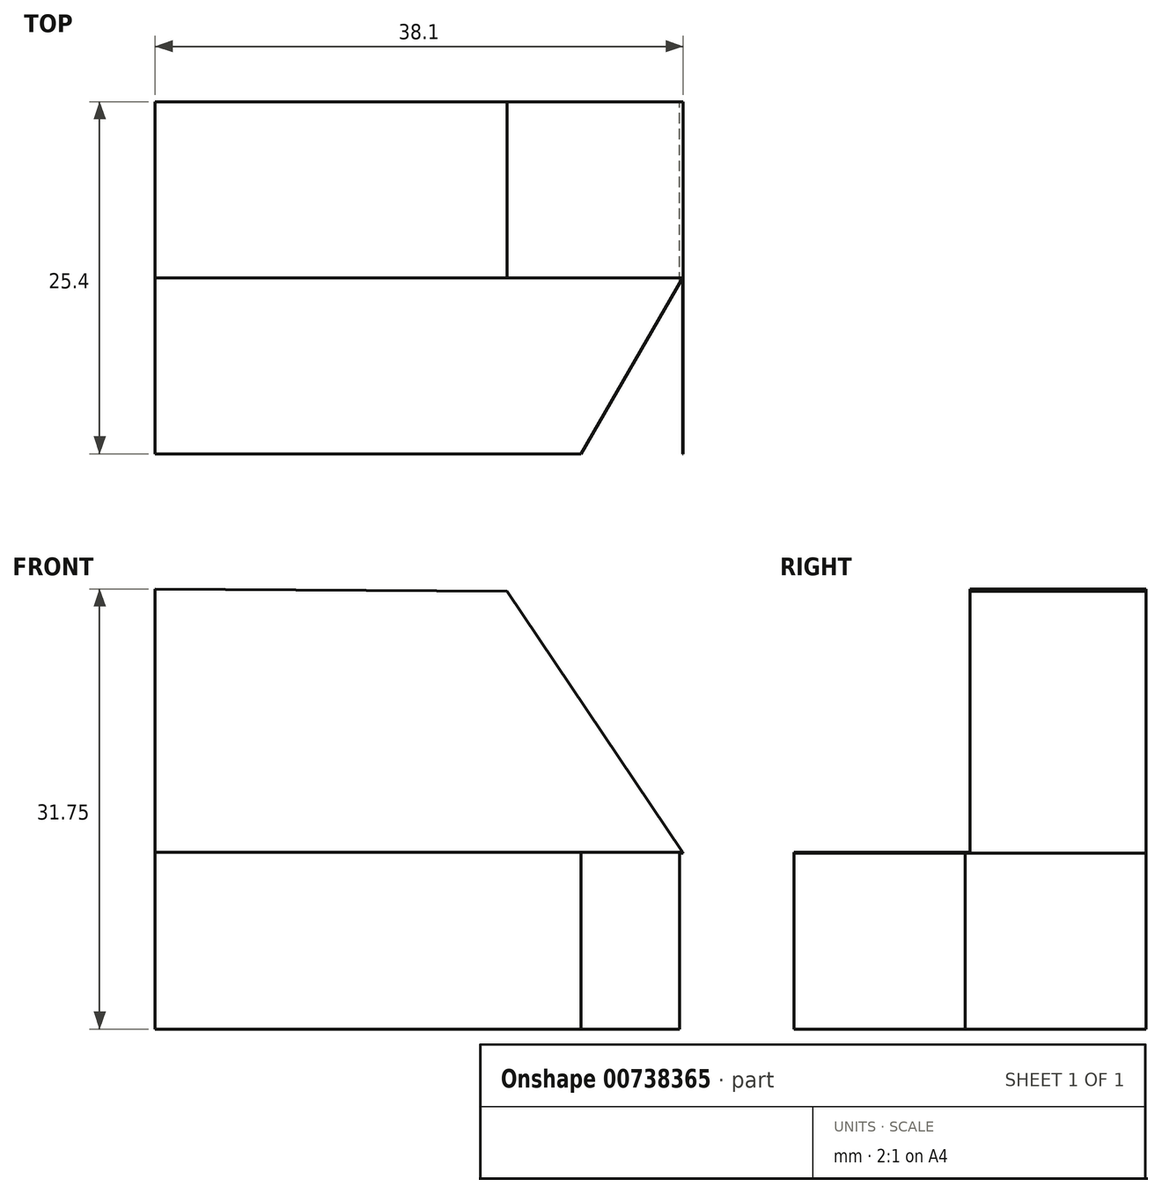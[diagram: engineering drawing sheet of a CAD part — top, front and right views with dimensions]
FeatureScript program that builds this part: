
annotation { "Feature Type Name" : "Feature", "Feature Type Description" : "" }
export const myFeature = defineFeature(function(context is Context, id is Id, definition is map)
    precondition{}
    {
        {
            var Q0;
            Q0=qCreatedBy(makeId("Front.planeOp"),FACE);
            var sketch = newSketch(context, id + "F0", { "sketchPlane" : qUnion([Q0])});
            skLineSegment(sketch, "E0", {"start": v(0, 31.75) * mm, "end": v(0, 0) * mm});
            skLineSegment(sketch, "E1", {"start": v(0, 0) * mm, "end": v(38.1, 0) * mm});
            skLineSegment(sketch, "E2", {"start": v(38.1, 0) * mm, "end": v(38.1, 12.7) * mm});
            skLineSegment(sketch, "E3", {"start": v(38.1, 12.7) * mm, "end": v(25.4, 31.59) * mm});
            skLineSegment(sketch, "E4", {"start": v(25.4, 31.59) * mm, "end": v(0, 31.75) * mm});
            skSolve(sketch);
        }
        {
            var Q0;
            Q0 = qSketchRegion(id + "F0", true);
            extrude(context, id + "F1", {"entities" : qUnion([Q0]), "depth" : 25.4 * mm, "offsetDistance" : 25.4 * mm});
        }
        {
            var Q0;
            Q0=qCreatedBy(makeId("Right.planeOp"),FACE);
            var sketch = newSketch(context, id + "F2", { "sketchPlane" : qUnion([Q0])});
            skLineSegment(sketch, "E5", {"start": v(-25.59, 31.92) * mm, "end": v(-12.92, 31.92) * mm});
            skLineSegment(sketch, "E6", {"start": v(-12.92, 31.92) * mm, "end": v(-12.92, 12.69) * mm});
            skLineSegment(sketch, "E7", {"start": v(-12.92, 12.69) * mm, "end": v(-25.4, 12.69) * mm});
            skLineSegment(sketch, "E8", {"start": v(-25.4, 12.69) * mm, "end": v(-25.59, 31.92) * mm});
            skSolve(sketch);
        }
        {
            var Q0;
            Q0=makeQuery(id+"F2.imprint","IMPRINT",FACE,{"disambiguationData":[TD([[makeQuery(id+"F2.imprint","IMPRINT",EDGE,{"derivedFrom":sQuery(id+"F2.wireOp",EDGE,"E5")}),-1.0]])]});
            extrude(context, id + "F3", {"entities" : qUnion([Q0]), "operationType" : NewBodyOperationType.REMOVE, "endBound" : BoundingType.THROUGH_ALL, "oppositeDirection" : true, "depth" : 25.4 * mm, "offsetDistance" : 25.4 * mm});
        }
        {
            var Q0;
            Q0 = qSketchRegion(id + "F2", true);
            var Q1;
            Q1=makeQuery(id+"F1.opExtrude","SWEPT_FACE",FACE,{"disambiguationData":[OSD([sQuery(id+"F0.wireOp",EDGE,"E0")])]});
            extrude(context, id + "F4", {"entities" : qUnion([Q0, Q1]), "operationType" : NewBodyOperationType.REMOVE, "oppositeDirection" : true, "depth" : 25.4 * mm, "offsetDistance" : 25.4 * mm});
        }
        {
            var Q0;
            Q0=makeQuery(id+"F1.opExtrude","SWEPT_FACE",FACE,{"disambiguationData":[OSD([sQuery(id+"F0.wireOp",EDGE,"E0")])]});
            var sketch = newSketch(context, id + "F5", { "sketchPlane" : qUnion([Q0])});
            skLineSegment(sketch, "E9", {"start": v(12.7, 31.75) * mm, "end": v(12.7, 12.77) * mm});
            skLineSegment(sketch, "E10", {"start": v(12.7, 12.77) * mm, "end": v(26.84, 12.77) * mm});
            skSolve(sketch);
        }
        {
            var Q0;
            Q0 = qSketchRegion(id + "F5", true);
            var Q1;
            {var subQ0=sQuery(id+"F5.wireOp",EDGE,"E9");Q1=makeQuery(id+"F5.imprint","IMPRINT",FACE,{"disambiguationData":[TD([[makeQuery(id+"F5.imprint","IMPRINT",EDGE,{"derivedFrom":subQ0}),1.0]])]});}
            extrude(context, id + "F6", {"entities" : qUnion([Q0, Q1]), "operationType" : NewBodyOperationType.REMOVE, "endBound" : BoundingType.THROUGH_ALL, "oppositeDirection" : true, "depth" : 25.4 * mm, "offsetDistance" : 25.4 * mm});
        }
        {
            var Q0;
            Q0=makeQuery(id+"F6.boolean.opBoolean","COPY",FACE,{"derivedFrom":makeQuery(id+"F6.opExtrude","SWEPT_FACE",FACE,{"disambiguationData":[OSD([sQuery(id+"F5.wireOp",EDGE,"E10")])]})});
            var sketch = newSketch(context, id + "F7", { "sketchPlane" : qUnion([Q0])});
            skLineSegment(sketch, "E11", {"start": v(38.06, -12.7) * mm, "end": v(30.73, -25.4) * mm});
            skSolve(sketch);
        }
        {
            var Q0;
            Q0 = qSketchRegion(id + "F7", true);
            var Q1;
            {var subQ0=sQuery(id+"F7.wireOp",EDGE,"E11");Q1=makeQuery(id+"F7.imprint","IMPRINT",FACE,{"disambiguationData":[TD([[makeQuery(id+"F7.imprint","IMPRINT",EDGE,{"derivedFrom":subQ0}),1.0]])]});}
            extrude(context, id + "F8", {"entities" : qUnion([Q0, Q1]), "operationType" : NewBodyOperationType.REMOVE, "oppositeDirection" : true, "depth" : 25.4 * mm, "offsetDistance" : 25.4 * mm});
        }
        {
            var Q0;
            Q0=makeQuery(id+"F1.opExtrude","SWEPT_FACE",FACE,{"disambiguationData":[OSD([sQuery(id+"F0.wireOp",EDGE,"E2")])]});
            var sketch = newSketch(context, id + "F9", { "sketchPlane" : qUnion([Q0])});
            skSolve(sketch);
        }
        {
            var Q0;
            {var subQ0=sQuery(id+"F0.wireOp",EDGE,"E2");Q0=makeQuery(id+"F9.imprint","IMPRINT",FACE,{"disambiguationData":[TD([[makeQuery(id+"F9.imprint","IMPRINT",EDGE,{"derivedFrom":makeQuery(id+"F1.opExtrude","CAP_EDGE",EDGE,{"disambiguationData":[OSD([subQ0])],"isStart":true})}),1.0]])]});}
            extrude(context, id + "F10", {"entities" : qUnion([Q0]), "operationType" : NewBodyOperationType.REMOVE, "oppositeDirection" : true, "depth" : 0.25 * mm, "offsetDistance" : 25.4 * mm});
        }
    });
